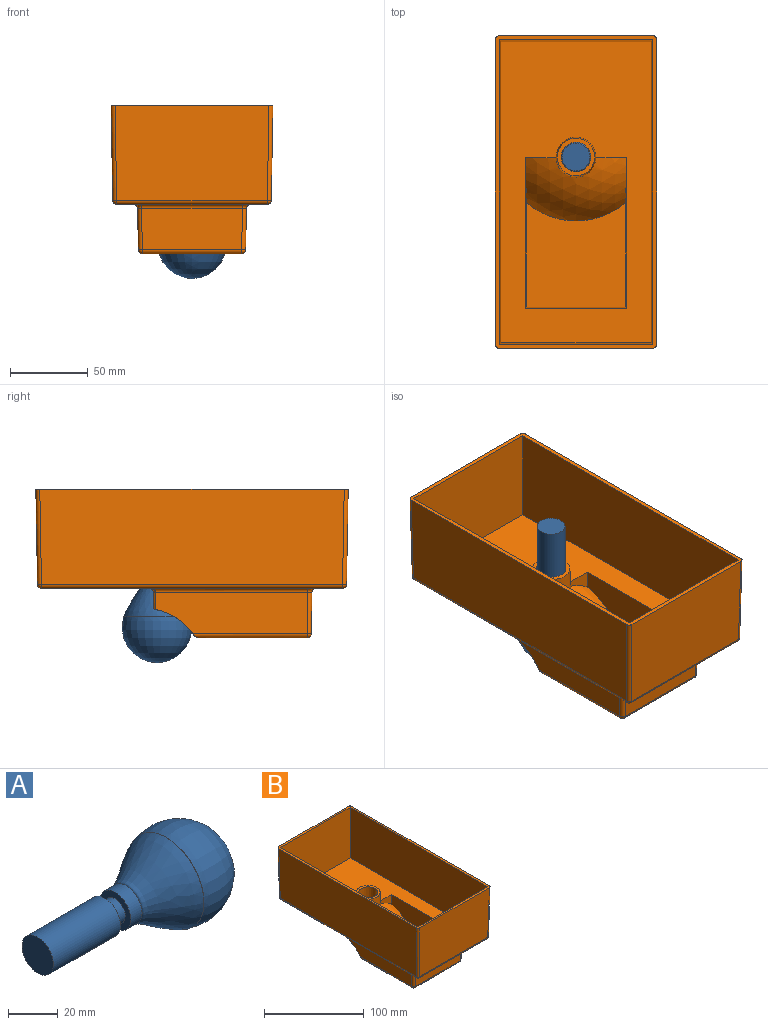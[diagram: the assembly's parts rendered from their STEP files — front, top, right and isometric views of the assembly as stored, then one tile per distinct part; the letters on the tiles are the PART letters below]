
ASSEMBLY  parts=2 mates=1
PART A: 10 faces, bbox 102.3x44.5x44.5 mm
  f0: revolved ~42.65x42.65mm, area 2512.1mm2, adj f2,f4
  f1: revolved ~44.52x44.52mm, area 4084.8mm2, adj f2
  f2: cone r=21.32mm half-angle=72.1deg, axis (-1,0,0), area 18.6mm2, adj f0,f1
  f3: plane 17.78x17.78mm, normal (-1,0,0), area 145.7mm2, adj f5,f6
  f4: plane 17.78x17.78mm, normal (1,0,0), area 38.1mm2, adj f0,f5
  f5: cylinder r=8.89mm len=17.78mm, axis (-1,0,0), area 354.7mm2, adj f3,f4
  f6: cylinder r=5.71mm len=11.43mm, axis (1,0,0), area 209.8mm2, adj f3,f9
  f7: cylinder r=8.89mm len=38.1mm, axis (1,0,0), area 2128.2mm2, adj f8,f9
  f8: plane 17.78x17.78mm, normal (-1,0,0), area 248.3mm2, adj f7
  f9: plane 17.78x17.78mm, normal (1,0,0), area 145.7mm2, adj f6,f7
PART B: 61 faces, bbox 115.7x212.2x112 mm
  f0: cone r=10.22mm half-angle=2deg, axis (0,0,-1), area 998.9mm2, adj f29,f30
  f1: cone r=12.76mm half-angle=2deg, axis (0,0,-1), area 1589.6mm2, adj f17,f18,f19,f25,f29
  f2: plane 200.37x103.85mm, normal (0,0,1), area 1514mm2, adj f7,f8,f9,f10,f21,f22,f23,f24
  f3: plane 18.77x10.78mm, normal (0,1,-0.02), area 79.8mm2, adj f5,f30,f42,f59
  f4: plane 18.76x10.77mm, normal (0,1,-0.02), area 79.8mm2, adj f5,f30,f33,f57
  f5: sphere r=50.97mm, area 3065.1mm2, adj f3,f4,f6,f15,f16,f30,f31,f34
  f6: plane 69.52x63.75mm, normal (0,0,-1), area 3890.8mm2, adj f5,f31,f34,f35
  f7: plane 195.26x61mm, normal (1,0,-0.02), area 11848.4mm2, adj f2,f50,f54,f56
  f8: plane 98.74x61mm, normal (0,1,-0.02), area 5959.4mm2, adj f2,f47,f53,f56
  f9: plane 195.26x61mm, normal (-1,0,-0.02), area 11848.4mm2, adj f2,f45,f47,f48
  f10: plane 98.74x61mm, normal (0,-1,-0.02), area 5959.4mm2, adj f2,f45,f49,f50
  f11: plane 193.13x96.61mm, normal (0,0,-1), area 10506.4mm2, adj f30,f33,f37,f39,f41,f42,f43,f44
  f12: plane 97.78x26.84mm, normal (-1,0,-0.02), area 2364.4mm2, adj f15,f31,f36,f37,f57
  f13: plane 97.78x26.84mm, normal (1,0,-0.02), area 2364.4mm2, adj f16,f34,f40,f44,f59
  f14: plane 64.68x26.76mm, normal (0,-1,-0.02), area 1718.6mm2, adj f35,f36,f40,f41
  f15: cylinder r=37.94mm len=25.8mm, axis (1,0,0), area 15.7mm2, adj f5,f12,f31,f57
  f16: cylinder r=37.94mm len=25.8mm, axis (1,0,0), area 15.7mm2, adj f5,f13,f34,f59
  f17: plane 20.34x12.08mm, normal (0,-1,0.02), area 117mm2, adj f1,f19,f25,f27
  f18: plane 20.34x12.08mm, normal (0,-1,0.02), area 117mm2, adj f1,f19,f25,f26
  f19: sphere r=53.51mm, area 2732.4mm2, adj f1,f17,f18,f20,f26,f27
  f20: plane 79.14x75.62mm, normal (0,0,1), area 3773.4mm2, adj f19,f26,f27,f28
  f21: plane 195.26x60.96mm, normal (-1,0,0.02), area 11839.7mm2, adj f2,f22,f24,f25
  f22: plane 98.74x60.96mm, normal (0,-1,0.02), area 5955mm2, adj f2,f21,f23,f25
  f23: plane 195.26x60.96mm, normal (1,0,0.02), area 11839.7mm2, adj f2,f22,f24,f25
  f24: plane 98.74x60.96mm, normal (0,1,0.02), area 5955mm2, adj f2,f21,f23,f25
  f25: plane 193.13x96.61mm, normal (0,0,1), area 12130.2mm2, adj f1,f17,f18,f21,f22,f23,f24,f26
  f26: plane 96.75x31.89mm, normal (1,0,0.02), area 2676.9mm2, adj f18,f19,f20,f25,f28
  f27: plane 96.75x31.89mm, normal (-1,0,0.02), area 2676.9mm2, adj f17,f19,f20,f25,f28
  f28: plane 64.86x31.75mm, normal (0,1,0.02), area 2042mm2, adj f20,f25,f26,f27
  f29: plane 24.04x24.04mm, normal (0,0,1), area 171.7mm2, adj f0,f1
  f30: bspline ~32.23x32.21mm, area 692.3mm2, adj f0,f3,f4,f5,f11,f33,f42
  f31: cylinder r=2.54mm len=73.2mm, axis (0,-1,0), area 282.4mm2, adj f5,f6,f12,f15,f32
  f32: sphere r=2.54mm, area 13.6mm2, adj f31,f35,f36
  f33: cylinder r=2.54mm len=25.65mm, axis (1,0,0), area 86.7mm2, adj f4,f11,f30,f58
  f34: cylinder r=2.54mm len=73.2mm, axis (0,-1,0), area 282.4mm2, adj f5,f6,f13,f16,f38
  f35: cylinder r=2.54mm len=63.75mm, axis (1,0,0), area 251.5mm2, adj f6,f14,f32,f38
  f36: cylinder r=2.54mm len=26.78mm, axis (-0.02,-0.02,1), area 106.8mm2, adj f12,f14,f32,f39
  f37: cylinder r=2.54mm len=101.51mm, axis (0,-1,0), area 393mm2, adj f11,f12,f39,f58
  f38: sphere r=2.54mm, area 9.9mm2, adj f34,f35,f40
  f39: bspline ~5.08x5.08mm, area 21.5mm2, adj f11,f36,f37,f41
  f40: cylinder r=2.54mm len=26.78mm, axis (0.02,-0.02,1), area 106.8mm2, adj f13,f14,f38,f43
  f41: cylinder r=2.54mm len=64.68mm, axis (1,0,0), area 255.2mm2, adj f11,f14,f39,f43
  f42: cylinder r=2.54mm len=25.65mm, axis (1,0,0), area 86.7mm2, adj f3,f11,f30,f60
  f43: bspline ~5.08x5.08mm, area 21.5mm2, adj f11,f40,f41,f44
  f44: cylinder r=2.54mm len=101.51mm, axis (0,-1,0), area 393mm2, adj f11,f13,f43,f60
  f45: cylinder r=2.54mm len=61.02mm, axis (0.02,0.02,-1), area 243.4mm2, adj f2,f9,f10,f46
  f46: sphere r=2.54mm, area 10mm2, adj f45,f48,f49
  f47: cylinder r=2.54mm len=61.02mm, axis (0.02,-0.02,-1), area 243.4mm2, adj f2,f8,f9,f51
  f48: cylinder r=2.54mm len=193.13mm, axis (0,1,0), area 762mm2, adj f9,f11,f46,f51
  f49: cylinder r=2.54mm len=96.61mm, axis (1,0,0), area 381.2mm2, adj f10,f11,f46,f52
  f50: cylinder r=2.54mm len=61.02mm, axis (-0.02,0.02,-1), area 243.4mm2, adj f2,f7,f10,f52
  f51: sphere r=2.54mm, area 6.3mm2, adj f47,f48,f53
  f52: sphere r=2.54mm, area 10mm2, adj f49,f50,f54
  f53: cylinder r=2.54mm len=96.61mm, axis (1,0,0), area 381.2mm2, adj f8,f11,f51,f55
  f54: cylinder r=2.54mm len=193.13mm, axis (0,1,0), area 762mm2, adj f7,f11,f52,f55
  f55: sphere r=2.54mm, area 6.3mm2, adj f53,f54,f56
  f56: cylinder r=2.54mm len=61.02mm, axis (-0.02,-0.02,-1), area 243.4mm2, adj f2,f7,f8,f55
  f57: cylinder r=1.27mm len=11.1mm, axis (-0.02,0.02,1), area 21.7mm2, adj f4,f5,f12,f15,f58
  f58: bspline ~3.81x3.81mm, area 3.4mm2, adj f33,f37,f57
  f59: cylinder r=1.27mm len=11.1mm, axis (0.02,0.02,1), area 21.7mm2, adj f3,f5,f13,f16,f60
  f60: bspline ~3.81x3.81mm, area 3.4mm2, adj f42,f44,f59
PLACE A rot(axis=(0.58,0.58,-0.58),120deg) t=(47.26,21.62,75.1)mm
PLACE B t=(47.26,-1.74,100.26)mm fixed
MATE slider A.f7 <-> B.f0  axis (0,0,-1) through (47.26,21.62,135.9)mm
